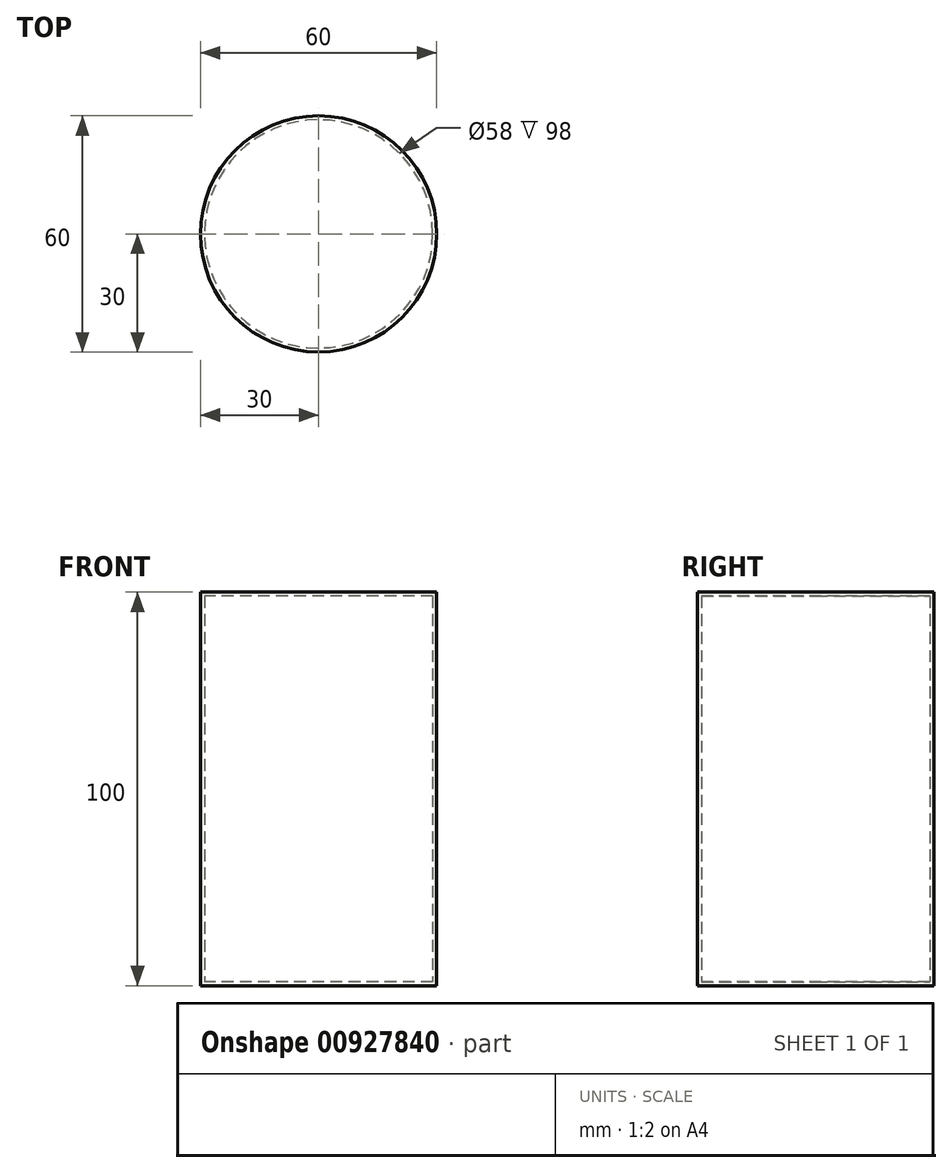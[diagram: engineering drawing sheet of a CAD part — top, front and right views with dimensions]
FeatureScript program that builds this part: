
annotation { "Feature Type Name" : "Feature", "Feature Type Description" : "" }
export const myFeature = defineFeature(function(context is Context, id is Id, definition is map)
    precondition{}
    {
        {
            var Q0;
            Q0=qCreatedBy(makeId("Top.planeOp"),FACE);
            var sketch = newSketch(context, id + "F0", { "sketchPlane" : qUnion([Q0])});
            skCircle(sketch, "E0", {"center": v(0, 0) * mm, "radius": 30 * mm});
            skSolve(sketch);
        }
        {
            var Q0;
            Q0 = qSketchRegion(id + "F0", true);
            extrude(context, id + "F1", {"entities" : qUnion([Q0]), "endBound" : BoundingType.SYMMETRIC, "depth" : 100 * mm, "offsetDistance" : 25 * mm});
        }
        {
            var Q0;
            Q0=qCreatedBy(makeId("Top.planeOp"),FACE);
            var sketch = newSketch(context, id + "F2", { "sketchPlane" : qUnion([Q0])});
            skCircle(sketch, "E1", {"center": v(0, 0) * mm, "radius": 29 * mm});
            skSolve(sketch);
        }
        {
            var Q0;
            Q0 = qSketchRegion(id + "F2", true);
            extrude(context, id + "F3", {"entities" : qUnion([Q0]), "endBound" : BoundingType.SYMMETRIC, "depth" : 98 * mm, "offsetDistance" : 25 * mm});
        }
        {
            var Q0;
            Q0=makeQuery(id+"F3.opExtrude","SWEPT_BODY",BODY,{"disambiguationData":[OSD([sQuery(id+"F2.wireOp",EDGE,"E1")])]});
            var Q1;
            Q1=makeQuery(id+"F1.opExtrude","SWEPT_BODY",BODY,{"disambiguationData":[OSD([sQuery(id+"F0.wireOp",EDGE,"E0")])]});
            booleanBodies(context, id + "F4", {"operationType" : BooleanOperationType.SUBTRACTION, "tools" : qUnion([Q0]), "targets" : qUnion([Q1])});
        }
    });
